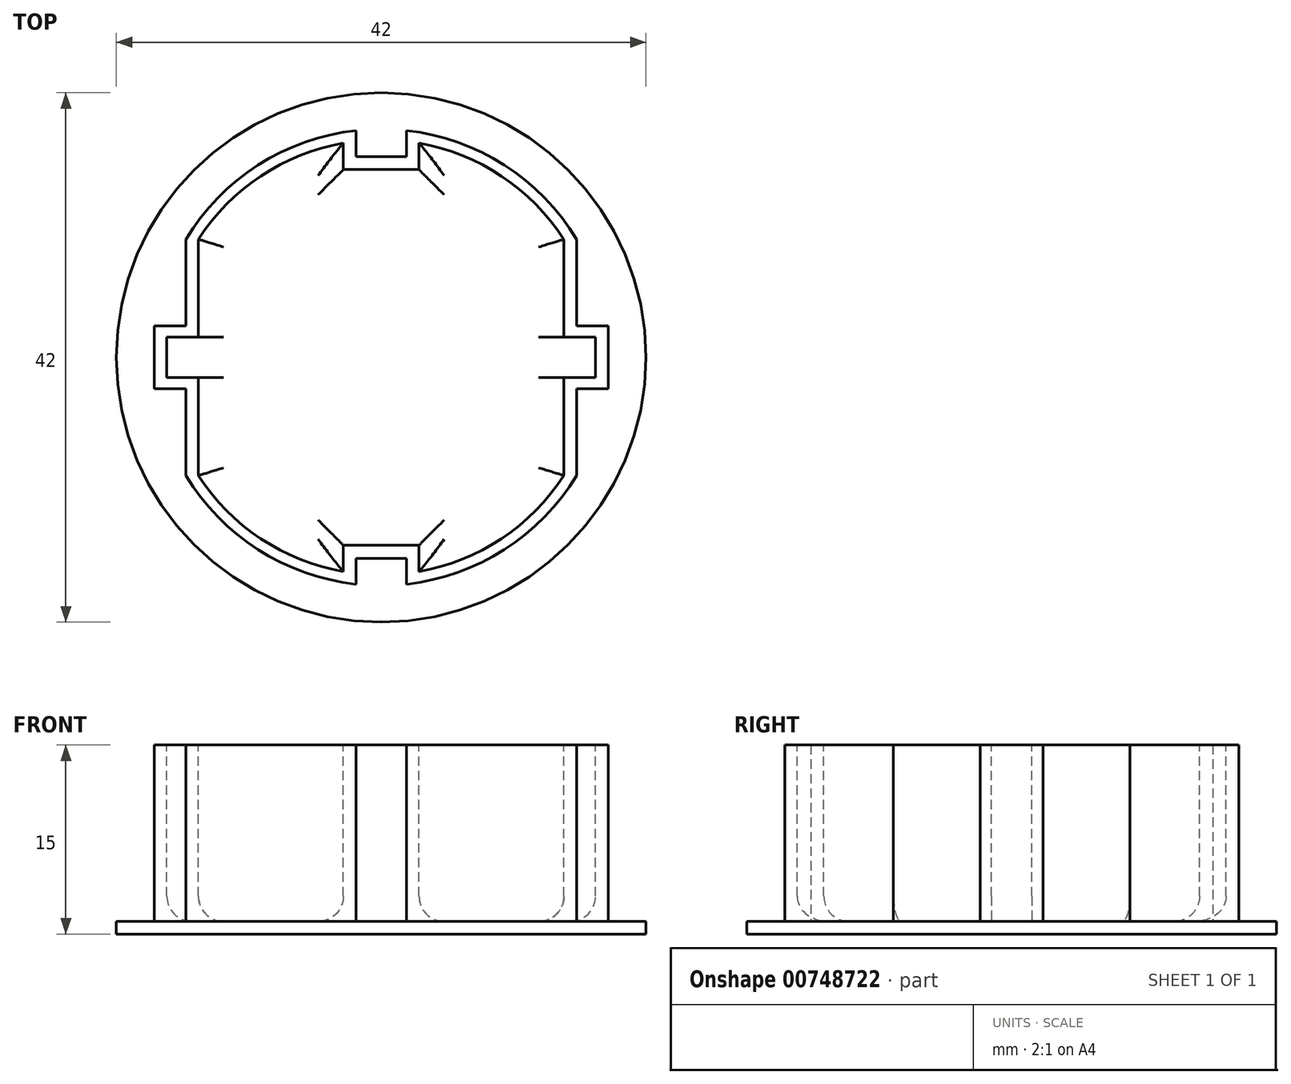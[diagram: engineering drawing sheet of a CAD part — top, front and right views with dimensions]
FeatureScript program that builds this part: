
annotation { "Feature Type Name" : "Feature", "Feature Type Description" : "" }
export const myFeature = defineFeature(function(context is Context, id is Id, definition is map)
    precondition{}
    {
        {
            var Q0;
            Q0=qCreatedBy(makeId("Top.planeOp"),FACE);
            var sketch = newSketch(context, id + "F0", { "sketchPlane" : qUnion([Q0])});
            skLineSegment(sketch, "E0.bottom", {"start": v(-18, -2.5) * mm, "end": v(-15.5, -2.5) * mm});
            skLineSegment(sketch, "E0.left", {"start": v(-18, -2.5) * mm, "end": v(-18, 0) * mm});
            skArc(sketch, "E1", {"start": v(-15.5, -9.37) * mm, "mid": v(-9.76, -15.26) * mm, "end": v(-2, -18) * mm});
            skLineSegment(sketch, "E2", {"start": v(-2, -18) * mm, "end": v(-2, -15.94) * mm});
            skLineSegment(sketch, "E3", {"start": v(-2, -15.94) * mm, "end": v(0, -15.94) * mm});
            skLineSegment(sketch, "E4", {"start": v(0, 0) * mm, "end": v(0, -15.94) * mm, "construction": true});
            skLineSegment(sketch, "E5", {"start": v(0, 0) * mm, "end": v(-18, 0) * mm, "construction": true});
            skLineSegment(sketch, "E6.MirrorCS", {"start": v(-18, 2.5) * mm, "end": v(-18, 0) * mm});
            skLineSegment(sketch, "E7.MirrorCS", {"start": v(-18, 2.5) * mm, "end": v(-15.5, 2.5) * mm});
            skArc(sketch, "E8.MirrorCS", {"start": v(-15.5, 9.37) * mm, "mid": v(-9.76, 15.26) * mm, "end": v(-2, 18) * mm});
            skLineSegment(sketch, "E9.MirrorCS", {"start": v(-2, 18) * mm, "end": v(-2, 15.94) * mm});
            skLineSegment(sketch, "E10.MirrorCS", {"start": v(-2, 15.94) * mm, "end": v(0, 15.94) * mm});
            skArc(sketch, "E11.MirrorCS", {"start": v(15.5, -9.37) * mm, "mid": v(9.76, -15.26) * mm, "end": v(2, -18) * mm});
            skLineSegment(sketch, "E12.MirrorCS", {"start": v(2, -15.94) * mm, "end": v(0, -15.94) * mm});
            skLineSegment(sketch, "E13.MirrorCS", {"start": v(2, -18) * mm, "end": v(2, -15.94) * mm});
            skLineSegment(sketch, "E14.MirrorCS", {"start": v(18, -2.5) * mm, "end": v(15.5, -2.5) * mm});
            skLineSegment(sketch, "E15.MirrorCS", {"start": v(18, -2.5) * mm, "end": v(18, 0) * mm});
            skLineSegment(sketch, "E16.MirrorCS", {"start": v(18, 2.5) * mm, "end": v(18, 0) * mm});
            skLineSegment(sketch, "E17.MirrorCS", {"start": v(18, 2.5) * mm, "end": v(15.5, 2.5) * mm});
            skArc(sketch, "E18.MirrorCS", {"start": v(15.5, 9.37) * mm, "mid": v(9.76, 15.26) * mm, "end": v(2, 18) * mm});
            skLineSegment(sketch, "E19.MirrorCS", {"start": v(2, 18) * mm, "end": v(2, 15.94) * mm});
            skLineSegment(sketch, "E20.MirrorCS", {"start": v(2, 15.94) * mm, "end": v(0, 15.94) * mm});
            skLineSegment(sketch, "E21", {"start": v(-15.5, -2.5) * mm, "end": v(-15.5, -9.37) * mm});
            skLineSegment(sketch, "E22.MirrorCS", {"start": v(15.5, -2.5) * mm, "end": v(15.5, -9.37) * mm});
            skLineSegment(sketch, "E23.MirrorCS", {"start": v(-15.5, 2.5) * mm, "end": v(-15.5, 9.37) * mm});
            skLineSegment(sketch, "E24.MirrorCS", {"start": v(15.5, 2.5) * mm, "end": v(15.5, 9.37) * mm});
            skCircle(sketch, "E25", {"center": v(0, 0) * mm, "radius": 21 * mm});
            skSolve(sketch);
        }
        {
            var Q0;
            Q0=makeQuery(id+"F0.imprint","IMPRINT",FACE,{"disambiguationData":[TD([[makeQuery(id+"F0.imprint","IMPRINT",EDGE,{"derivedFrom":sQuery(id+"F0.wireOp",EDGE,"E0.bottom")}),-1.0]])]});
            var Q1;
            Q1=makeQuery(id+"F0.imprint","IMPRINT",FACE,{"disambiguationData":[TD([[makeQuery(id+"F0.imprint","IMPRINT",EDGE,{"derivedFrom":sQuery(id+"F0.wireOp",EDGE,"E0.bottom")}),1.0]])]});
            extrude(context, id + "F1", {"entities" : qUnion([Q0, Q1]), "depth" : 1 * mm, "offsetDistance" : 25 * mm});
        }
        {
            var Q0;
            Q0=makeQuery(id+"F0.imprint","IMPRINT",FACE,{"disambiguationData":[TD([[makeQuery(id+"F0.imprint","IMPRINT",EDGE,{"derivedFrom":sQuery(id+"F0.wireOp",EDGE,"E0.bottom")}),1.0]])]});
            extrude(context, id + "F2", {"entities" : qUnion([Q0]), "operationType" : NewBodyOperationType.ADD, "depth" : 15 * mm, "offsetDistance" : 25 * mm});
        }
        {
            var Q0;
            Q0=makeQuery(id+"F2.opExtrude","CAP_FACE",FACE,{"disambiguationData":[OSD([sQuery(id+"F0.wireOp",EDGE,"E0.bottom"),sQuery(id+"F0.wireOp",EDGE,"E0.left"),sQuery(id+"F0.wireOp",EDGE,"E1"),sQuery(id+"F0.wireOp",EDGE,"E2"),sQuery(id+"F0.wireOp",EDGE,"E3"),sQuery(id+"F0.wireOp",EDGE,"E6.MirrorCS"),sQuery(id+"F0.wireOp",EDGE,"E7.MirrorCS"),sQuery(id+"F0.wireOp",EDGE,"E8.MirrorCS"),sQuery(id+"F0.wireOp",EDGE,"E9.MirrorCS"),sQuery(id+"F0.wireOp",EDGE,"E10.MirrorCS"),sQuery(id+"F0.wireOp",EDGE,"E11.MirrorCS"),sQuery(id+"F0.wireOp",EDGE,"E12.MirrorCS"),sQuery(id+"F0.wireOp",EDGE,"E13.MirrorCS"),sQuery(id+"F0.wireOp",EDGE,"E14.MirrorCS"),sQuery(id+"F0.wireOp",EDGE,"E15.MirrorCS"),sQuery(id+"F0.wireOp",EDGE,"E16.MirrorCS"),sQuery(id+"F0.wireOp",EDGE,"E17.MirrorCS"),sQuery(id+"F0.wireOp",EDGE,"E18.MirrorCS"),sQuery(id+"F0.wireOp",EDGE,"E19.MirrorCS"),sQuery(id+"F0.wireOp",EDGE,"E20.MirrorCS"),sQuery(id+"F0.wireOp",EDGE,"E21"),sQuery(id+"F0.wireOp",EDGE,"E22.MirrorCS"),sQuery(id+"F0.wireOp",EDGE,"E23.MirrorCS"),sQuery(id+"F0.wireOp",EDGE,"E24.MirrorCS")])],"isStart":false});
            var sketch = newSketch(context, id + "F3", { "sketchPlane" : qUnion([Q0])});
            skLineSegment(sketch, "E26.bottom", {"start": v(-17, -1.6) * mm, "end": v(-14.5, -1.6) * mm});
            skLineSegment(sketch, "E26.left", {"start": v(-17, -1.6) * mm, "end": v(-17, 0) * mm});
            skArc(sketch, "E27", {"start": v(-14.5, -9.37) * mm, "mid": v(-9.55, -14.38) * mm, "end": v(-3, -17) * mm});
            skLineSegment(sketch, "E28", {"start": v(-3, -17) * mm, "end": v(-3, -14.9) * mm});
            skLineSegment(sketch, "E29", {"start": v(-3, -14.9) * mm, "end": v(0, -14.9) * mm});
            skLineSegment(sketch, "E30", {"start": v(0, 0) * mm, "end": v(0, -14.9) * mm, "construction": true});
            skLineSegment(sketch, "E31", {"start": v(0, 0) * mm, "end": v(-17, 0) * mm, "construction": true});
            skLineSegment(sketch, "E32.MirrorCS", {"start": v(-17, 1.6) * mm, "end": v(-17, 0) * mm});
            skLineSegment(sketch, "E33.MirrorCS", {"start": v(-17, 1.6) * mm, "end": v(-14.5, 1.6) * mm});
            skArc(sketch, "E34.MirrorCS", {"start": v(-14.5, 9.37) * mm, "mid": v(-9.55, 14.38) * mm, "end": v(-3, 17) * mm});
            skLineSegment(sketch, "E35.MirrorCS", {"start": v(-3, 17) * mm, "end": v(-3, 14.9) * mm});
            skLineSegment(sketch, "E36.MirrorCS", {"start": v(-3, 14.9) * mm, "end": v(0, 14.9) * mm});
            skArc(sketch, "E37.MirrorCS", {"start": v(14.5, -9.37) * mm, "mid": v(9.55, -14.38) * mm, "end": v(3, -17) * mm});
            skLineSegment(sketch, "E38.MirrorCS", {"start": v(3, -14.9) * mm, "end": v(0, -14.9) * mm});
            skLineSegment(sketch, "E39.MirrorCS", {"start": v(3, -17) * mm, "end": v(3, -14.9) * mm});
            skLineSegment(sketch, "E40.MirrorCS", {"start": v(17, -1.6) * mm, "end": v(14.5, -1.6) * mm});
            skLineSegment(sketch, "E41.MirrorCS", {"start": v(17, -1.6) * mm, "end": v(17, 0) * mm});
            skLineSegment(sketch, "E42.MirrorCS", {"start": v(17, 1.6) * mm, "end": v(17, 0) * mm});
            skLineSegment(sketch, "E43.MirrorCS", {"start": v(17, 1.6) * mm, "end": v(14.5, 1.6) * mm});
            skArc(sketch, "E44.MirrorCS", {"start": v(14.5, 9.37) * mm, "mid": v(9.55, 14.38) * mm, "end": v(3, 17) * mm});
            skLineSegment(sketch, "E45.MirrorCS", {"start": v(3, 17) * mm, "end": v(3, 14.9) * mm});
            skLineSegment(sketch, "E46.MirrorCS", {"start": v(3, 14.9) * mm, "end": v(0, 14.9) * mm});
            skLineSegment(sketch, "E47", {"start": v(-14.5, -1.6) * mm, "end": v(-14.5, -9.37) * mm});
            skLineSegment(sketch, "E48.MirrorCS", {"start": v(14.5, -1.6) * mm, "end": v(14.5, -9.37) * mm});
            skLineSegment(sketch, "E49.MirrorCS", {"start": v(-14.5, 1.6) * mm, "end": v(-14.5, 9.37) * mm});
            skLineSegment(sketch, "E50.MirrorCS", {"start": v(14.5, 1.6) * mm, "end": v(14.5, 9.37) * mm});
            skSolve(sketch);
        }
        {
            var Q0;
            Q0=makeQuery(id+"F3.imprint","IMPRINT",FACE,{"disambiguationData":[TD([[makeQuery(id+"F3.imprint","IMPRINT",EDGE,{"derivedFrom":sQuery(id+"F3.wireOp",EDGE,"E26.bottom")}),1.0]])]});
            extrude(context, id + "F4", {"entities" : qUnion([Q0]), "operationType" : NewBodyOperationType.REMOVE, "oppositeDirection" : true, "depth" : 14 * mm, "offsetDistance" : 25 * mm});
        }
        {
            var Q0;
            Q0=makeQuery(id+"F4.boolean.opBoolean","COPY",EDGE,{"derivedFrom":makeQuery(id+"F4.opExtrude","CAP_EDGE",EDGE,{"disambiguationData":[OSD([sQuery(id+"F3.wireOp",EDGE,"E47")])],"isStart":false})});
            var Q1;
            Q1=makeQuery(id+"F4.boolean.opBoolean","COPY",EDGE,{"derivedFrom":makeQuery(id+"F4.opExtrude","CAP_EDGE",EDGE,{"disambiguationData":[OSD([sQuery(id+"F3.wireOp",EDGE,"E26.left"),sQuery(id+"F3.wireOp",EDGE,"E32.MirrorCS")])],"isStart":false})});
            var Q2;
            Q2=makeQuery(id+"F4.boolean.opBoolean","COPY",EDGE,{"derivedFrom":makeQuery(id+"F4.opExtrude","CAP_EDGE",EDGE,{"disambiguationData":[OSD([sQuery(id+"F3.wireOp",EDGE,"E49.MirrorCS")])],"isStart":false})});
            var Q3;
            Q3=makeQuery(id+"F4.boolean.opBoolean","COPY",EDGE,{"derivedFrom":makeQuery(id+"F4.opExtrude","CAP_EDGE",EDGE,{"disambiguationData":[OSD([sQuery(id+"F3.wireOp",EDGE,"E34.MirrorCS")])],"isStart":false})});
            var Q4;
            Q4=makeQuery(id+"F4.boolean.opBoolean","COPY",EDGE,{"derivedFrom":makeQuery(id+"F4.opExtrude","CAP_EDGE",EDGE,{"disambiguationData":[OSD([sQuery(id+"F3.wireOp",EDGE,"E27")])],"isStart":false})});
            var Q5;
            Q5=makeQuery(id+"F4.boolean.opBoolean","COPY",EDGE,{"derivedFrom":makeQuery(id+"F4.opExtrude","CAP_EDGE",EDGE,{"disambiguationData":[OSD([sQuery(id+"F3.wireOp",EDGE,"E37.MirrorCS")])],"isStart":false})});
            var Q6;
            Q6=makeQuery(id+"F4.boolean.opBoolean","COPY",EDGE,{"derivedFrom":makeQuery(id+"F4.opExtrude","CAP_EDGE",EDGE,{"disambiguationData":[OSD([sQuery(id+"F3.wireOp",EDGE,"E29"),sQuery(id+"F3.wireOp",EDGE,"E38.MirrorCS")])],"isStart":false})});
            var Q7;
            Q7=makeQuery(id+"F4.boolean.opBoolean","COPY",EDGE,{"derivedFrom":makeQuery(id+"F4.opExtrude","CAP_EDGE",EDGE,{"disambiguationData":[OSD([sQuery(id+"F3.wireOp",EDGE,"E48.MirrorCS")])],"isStart":false})});
            var Q8;
            Q8=makeQuery(id+"F4.boolean.opBoolean","COPY",EDGE,{"derivedFrom":makeQuery(id+"F4.opExtrude","CAP_EDGE",EDGE,{"disambiguationData":[OSD([sQuery(id+"F3.wireOp",EDGE,"E50.MirrorCS")])],"isStart":false})});
            var Q9;
            Q9=makeQuery(id+"F4.boolean.opBoolean","COPY",EDGE,{"derivedFrom":makeQuery(id+"F4.opExtrude","CAP_EDGE",EDGE,{"disambiguationData":[OSD([sQuery(id+"F3.wireOp",EDGE,"E41.MirrorCS"),sQuery(id+"F3.wireOp",EDGE,"E42.MirrorCS")])],"isStart":false})});
            var Q10;
            Q10=makeQuery(id+"F4.boolean.opBoolean","COPY",EDGE,{"derivedFrom":makeQuery(id+"F4.opExtrude","CAP_EDGE",EDGE,{"disambiguationData":[OSD([sQuery(id+"F3.wireOp",EDGE,"E44.MirrorCS")])],"isStart":false})});
            var Q11;
            Q11=makeQuery(id+"F4.boolean.opBoolean","COPY",EDGE,{"derivedFrom":makeQuery(id+"F4.opExtrude","CAP_EDGE",EDGE,{"disambiguationData":[OSD([sQuery(id+"F3.wireOp",EDGE,"E36.MirrorCS"),sQuery(id+"F3.wireOp",EDGE,"E46.MirrorCS")])],"isStart":false})});
            var Q12;
            Q12=makeQuery(id+"F4.boolean.opBoolean","COPY",EDGE,{"derivedFrom":makeQuery(id+"F4.opExtrude","CAP_EDGE",EDGE,{"disambiguationData":[OSD([sQuery(id+"F3.wireOp",EDGE,"E39.MirrorCS")])],"isStart":false})});
            var Q13;
            Q13=makeQuery(id+"F4.boolean.opBoolean","COPY",EDGE,{"derivedFrom":makeQuery(id+"F4.opExtrude","CAP_EDGE",EDGE,{"disambiguationData":[OSD([sQuery(id+"F3.wireOp",EDGE,"E28")])],"isStart":false})});
            var Q14;
            Q14=makeQuery(id+"F4.boolean.opBoolean","COPY",EDGE,{"derivedFrom":makeQuery(id+"F4.opExtrude","CAP_EDGE",EDGE,{"disambiguationData":[OSD([sQuery(id+"F3.wireOp",EDGE,"E45.MirrorCS")])],"isStart":false})});
            var Q15;
            Q15=makeQuery(id+"F4.boolean.opBoolean","COPY",EDGE,{"derivedFrom":makeQuery(id+"F4.opExtrude","CAP_EDGE",EDGE,{"disambiguationData":[OSD([sQuery(id+"F3.wireOp",EDGE,"E35.MirrorCS")])],"isStart":false})});
            fillet(context, id + "F5", {"entities" : qUnion([Q0, Q1, Q2, Q3, Q4, Q5, Q6, Q7, Q8, Q9, Q10, Q11, Q12, Q13, Q14, Q15]), "radius" : 2 * mm, "tangentPropagation" : true, "allowEdgeOverflow" : false});
        }
    });
